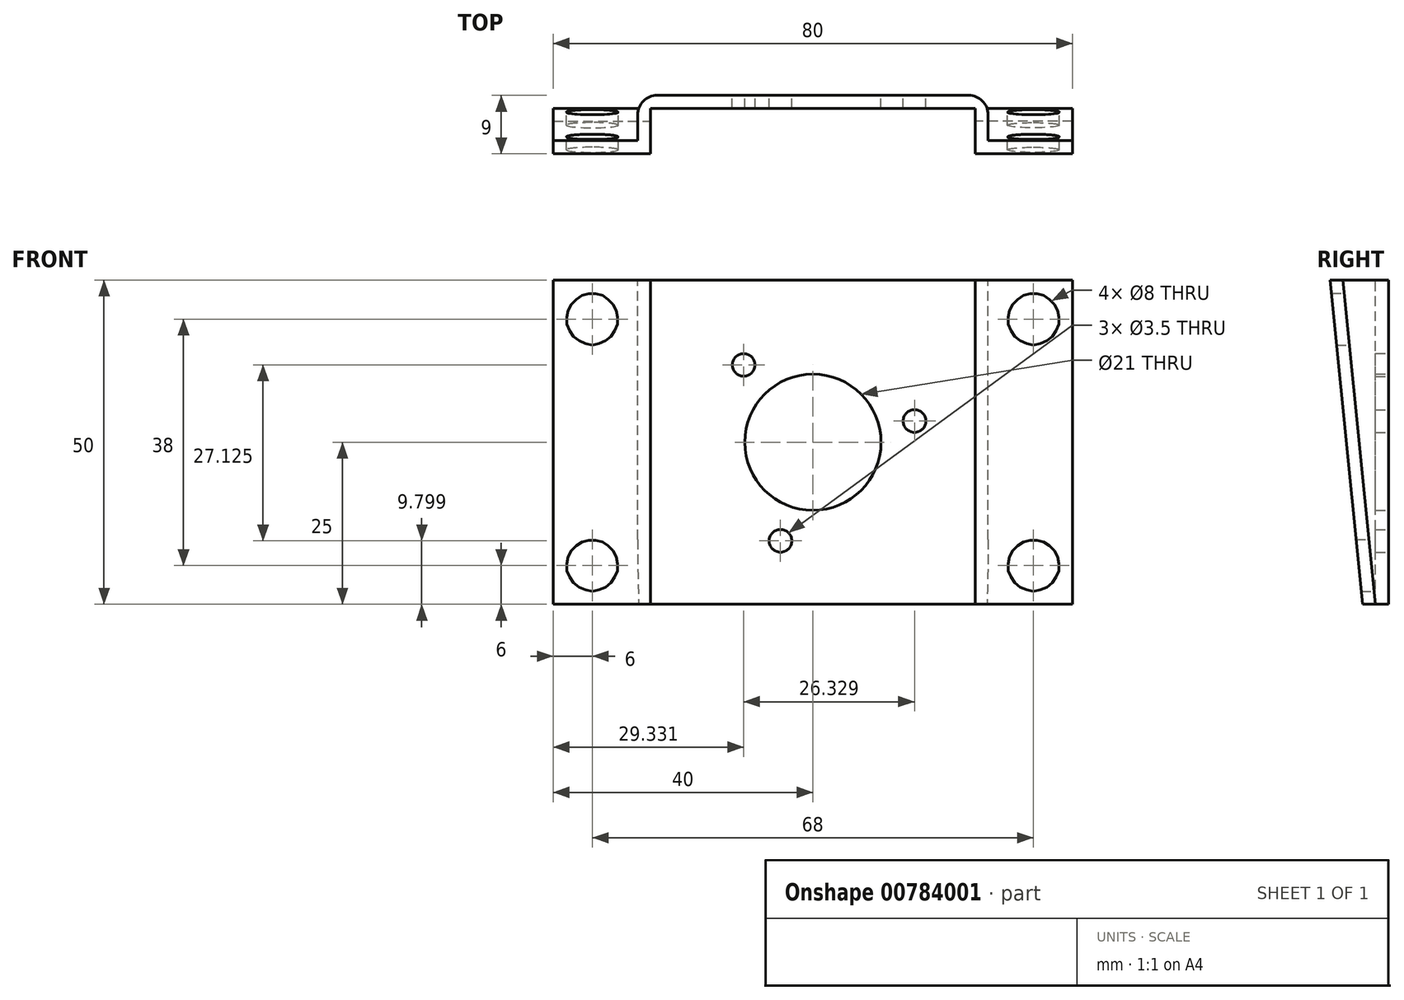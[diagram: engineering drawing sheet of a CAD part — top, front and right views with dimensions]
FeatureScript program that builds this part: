
annotation { "Feature Type Name" : "Feature", "Feature Type Description" : "" }
export const myFeature = defineFeature(function(context is Context, id is Id, definition is map)
    precondition{}
    {
        {
            var Q0;
            Q0=qCreatedBy(makeId("Front.planeOp"),FACE);
            var sketch = newSketch(context, id + "F0", { "sketchPlane" : qUnion([Q0])});
            skLineSegment(sketch, "E0.bottom", {"start": v(-25, -25) * mm, "end": v(25, -25) * mm});
            skLineSegment(sketch, "E0.top", {"start": v(-25, 25) * mm, "end": v(25, 25) * mm});
            skLineSegment(sketch, "E0.left", {"start": v(-25, -25) * mm, "end": v(-25, 25) * mm});
            skLineSegment(sketch, "E0.right", {"start": v(25, -25) * mm, "end": v(25, 25) * mm});
            skPoint(sketch, "E0.middle", {"position": v(0, 0) * mm});
            skCircle(sketch, "E1", {"center": v(0, 0) * mm, "radius": 10.5 * mm});
            skCircle(sketch, "E2", {"center": v(-10.67, 11.92) * mm, "radius": 1.75 * mm});
            skCircle(sketch, "E3.1.0", {"center": v(-5, -15.2) * mm, "radius": 1.75 * mm});
            skCircle(sketch, "E3.2.0", {"center": v(15.66, 3.28) * mm, "radius": 1.75 * mm});
            skLineSegment(sketch, "E4", {"start": v(-25, 25) * mm, "end": v(-25, -25) * mm});
            skSolve(sketch);
        }
        {
            var Q0;
            Q0 = qSketchRegion(id + "F0", true);
            extrude(context, id + "F1", {"entities" : qUnion([Q0]), "depth" : 2 * mm, "offsetDistance" : 25 * mm});
        }
        {
            var Q0;
            Q0=qCreatedBy(makeId("Right.planeOp"),FACE);
            var sketch = newSketch(context, id + "F2", { "sketchPlane" : qUnion([Q0])});
            skLineSegment(sketch, "E5", {"start": v(-2, 25) * mm, "end": v(0, 25) * mm});
            skLineSegment(sketch, "E6", {"start": v(0, 25) * mm, "end": v(0, -25) * mm});
            skLineSegment(sketch, "E7", {"start": v(0, -25) * mm, "end": v(-2, -25) * mm});
            skLineSegment(sketch, "E8", {"start": v(-2, -25) * mm, "end": v(-7, 25) * mm});
            skLineSegment(sketch, "E9", {"start": v(-7, 25) * mm, "end": v(-2, 25) * mm});
            skSolve(sketch);
        }
        {
            var Q0;
            Q0=makeQuery(id+"F2.imprint","IMPRINT",FACE,{"disambiguationData":[TD([[makeQuery(id+"F2.imprint","IMPRINT",EDGE,{"derivedFrom":sQuery(id+"F2.wireOp",EDGE,"E5")}),-1.0]])]});
            extrude(context, id + "F3", {"entities" : qUnion([Q0]), "operationType" : NewBodyOperationType.ADD, "depth" : 27 * mm, "offsetDistance" : 25 * mm, "hasSecondDirection" : true, "secondDirectionOppositeDirection" : false, "secondDirectionDepth" : 25 * mm});
        }
        {
            var Q0;
            Q0=qCreatedBy(makeId("Right.planeOp"),FACE);
            var sketch = newSketch(context, id + "F4", { "sketchPlane" : qUnion([Q0])});
            skLineSegment(sketch, "E10", {"start": v(0, 25) * mm, "end": v(-2, 25) * mm});
            skLineSegment(sketch, "E11", {"start": v(-2, 25) * mm, "end": v(-7, 25) * mm});
            skLineSegment(sketch, "E12", {"start": v(-7, 25) * mm, "end": v(-2, -25) * mm});
            skLineSegment(sketch, "E13", {"start": v(-2, -25) * mm, "end": v(0, -25) * mm});
            skLineSegment(sketch, "E14", {"start": v(0, -25) * mm, "end": v(0, 25) * mm});
            skSolve(sketch);
        }
        {
            var Q0;
            Q0=makeQuery(id+"F4.imprint","IMPRINT",FACE,{"disambiguationData":[TD([[makeQuery(id+"F4.imprint","IMPRINT",EDGE,{"derivedFrom":sQuery(id+"F4.wireOp",EDGE,"E10")}),1.0]])]});
            extrude(context, id + "F5", {"entities" : qUnion([Q0]), "operationType" : NewBodyOperationType.ADD, "oppositeDirection" : true, "depth" : 27 * mm, "offsetDistance" : 25 * mm, "hasSecondDirection" : true, "secondDirectionOppositeDirection" : true, "secondDirectionDepth" : 25 * mm});
        }
        {
            var Q0;
            Q0=qCreatedBy(makeId("Right.planeOp"),FACE);
            var sketch = newSketch(context, id + "F6", { "sketchPlane" : qUnion([Q0])});
            skLineSegment(sketch, "E15", {"start": v(-7, 25) * mm, "end": v(-2, -25) * mm});
            skLineSegment(sketch, "E16", {"start": v(-2, -25) * mm, "end": v(-4, -25) * mm});
            skLineSegment(sketch, "E17", {"start": v(-4, -25) * mm, "end": v(-9, 25) * mm});
            skLineSegment(sketch, "E18", {"start": v(-9, 25) * mm, "end": v(-7, 25) * mm});
            skSolve(sketch);
        }
        {
            var Q0;
            Q0 = qSketchRegion(id + "F6", true);
            extrude(context, id + "F7", {"entities" : qUnion([Q0]), "operationType" : NewBodyOperationType.ADD, "depth" : 40 * mm, "offsetDistance" : 25 * mm, "hasSecondDirection" : true, "secondDirectionOppositeDirection" : false, "secondDirectionDepth" : 25 * mm});
        }
        {
            var Q0;
            Q0 = qSketchRegion(id + "F6", true);
            extrude(context, id + "F8", {"entities" : qUnion([Q0]), "operationType" : NewBodyOperationType.ADD, "oppositeDirection" : true, "depth" : 40 * mm, "offsetDistance" : 25 * mm, "hasSecondDirection" : true, "secondDirectionOppositeDirection" : true, "secondDirectionDepth" : 25 * mm});
        }
        {
            var Q0;
            Q0=qCreatedBy(makeId("Front.planeOp"),FACE);
            var sketch = newSketch(context, id + "F9", { "sketchPlane" : qUnion([Q0])});
            skPoint(sketch, "E19", {"position": v(-34, 19) * mm});
            skPoint(sketch, "E20", {"position": v(-34, -19) * mm});
            skPoint(sketch, "E21", {"position": v(34, -19) * mm});
            skPoint(sketch, "E22", {"position": v(34, 19) * mm});
            skSolve(sketch);
        }
        {
            var Q0;
            Q0=sQuery(id+"F9.wireOp",VERTEX,"E19");
            var Q1;
            Q1=sQuery(id+"F9.wireOp",VERTEX,"E20");
            var Q2;
            Q2=sQuery(id+"F9.wireOp",VERTEX,"E21");
            var Q3;
            Q3=sQuery(id+"F9.wireOp",VERTEX,"E22");
            var Q4;
            Q4=makeQuery(id+"F1.opExtrude","SWEPT_BODY",BODY,{"disambiguationData":[OSD([sQuery(id+"F0.wireOp",EDGE,"E0.bottom"),sQuery(id+"F0.wireOp",EDGE,"E0.top"),sQuery(id+"F0.wireOp",EDGE,"E0.right"),sQuery(id+"F0.wireOp",EDGE,"E1"),sQuery(id+"F0.wireOp",EDGE,"E2"),sQuery(id+"F0.wireOp",EDGE,"E3.1.0"),sQuery(id+"F0.wireOp",EDGE,"E3.2.0"),sQuery(id+"F0.wireOp",EDGE,"E4")])]});
            hole(context, id + "F10", {"style" : HoleStyle.SIMPLE, "endStyle" : HoleEndStyle.THROUGH, "oppositeDirection" : true, "holeDiameter" : 8 * mm, "majorDiameter" : 5 * mm, "isTappedThrough" : true, "tappedDepth" : 12 * mm, "tapClearance" : 3, "locations" : qUnion([Q0, Q1, Q2, Q3]), "scope" : qUnion([Q4])});
        }
        {
            var Q0;
            Q0=makeQuery(id+"F5.opExtrude","CAP_EDGE",EDGE,{"disambiguationData":[OSD([sQuery(id+"F4.wireOp",EDGE,"E14")])],"isStart":false});
            var Q1;
            Q1=makeQuery(id+"F3.opExtrude","CAP_EDGE",EDGE,{"disambiguationData":[OSD([sQuery(id+"F2.wireOp",EDGE,"E6")])],"isStart":false});
            var Q2;
            Q2=makeQuery(id+"F1.opExtrude","CAP_EDGE",EDGE,{"disambiguationData":[OSD([sQuery(id+"F0.wireOp",EDGE,"E0.right")])],"isStart":false});
            var Q3;
            Q3=makeQuery(id+"F1.opExtrude","CAP_EDGE",EDGE,{"disambiguationData":[OSD([sQuery(id+"F0.wireOp",EDGE,"E4")])],"isStart":false});
            fillet(context, id + "F11", {"entities" : qUnion([Q0, Q1, Q2, Q3]), "radius" : 3 * mm, "tangentPropagation" : true, "allowEdgeOverflow" : false});
        }
    });
